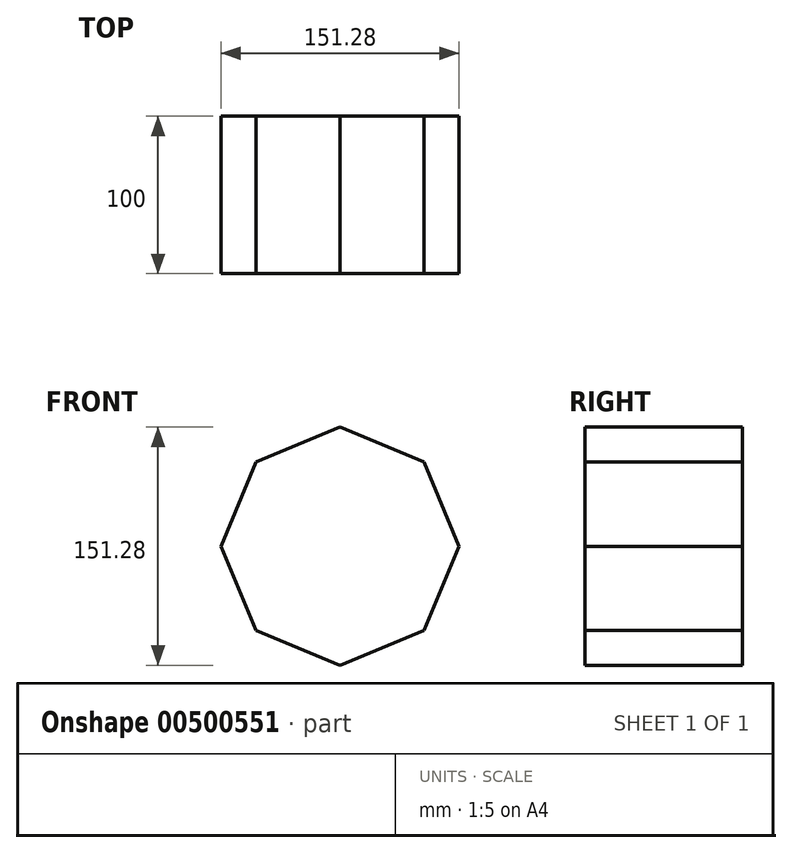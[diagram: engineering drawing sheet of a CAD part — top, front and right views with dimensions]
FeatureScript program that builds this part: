
annotation { "Feature Type Name" : "Feature", "Feature Type Description" : "" }
export const myFeature = defineFeature(function(context is Context, id is Id, definition is map)
    precondition{}
    {
        {
            var Q0;
            Q0=qCreatedBy(makeId("Front.planeOp"),FACE);
            var sketch = newSketch(context, id + "F0", { "sketchPlane" : qUnion([Q0])});
            skCircle(sketch, "E0.cCircle", {"center": v(0, 0) * mm, "radius": 75.64 * mm, "construction": true});
            skLineSegment(sketch, "E0.0", {"start": v(0, 75.64) * mm, "end": v(53.48, 53.48) * mm});
            skLineSegment(sketch, "E0.1", {"start": v(53.48, 53.48) * mm, "end": v(75.64, 0) * mm});
            skLineSegment(sketch, "E0.2", {"start": v(75.64, 0) * mm, "end": v(53.48, -53.48) * mm});
            skLineSegment(sketch, "E0.3", {"start": v(53.48, -53.48) * mm, "end": v(0, -75.64) * mm});
            skLineSegment(sketch, "E0.4", {"start": v(0, -75.64) * mm, "end": v(-53.48, -53.48) * mm});
            skLineSegment(sketch, "E0.5", {"start": v(-53.48, -53.48) * mm, "end": v(-75.64, 0) * mm});
            skLineSegment(sketch, "E0.6", {"start": v(-75.64, 0) * mm, "end": v(-53.48, 53.48) * mm});
            skLineSegment(sketch, "E0.7", {"start": v(-53.48, 53.48) * mm, "end": v(0, 75.64) * mm});
            skSolve(sketch);
        }
        {
            var Q0;
            Q0=makeQuery(id+"F0.imprint","IMPRINT",FACE,{"disambiguationData":[TD([[makeQuery(id+"F0.imprint","IMPRINT",EDGE,{"derivedFrom":sQuery(id+"F0.wireOp",EDGE,"E0.0")}),-1.0]])]});
            extrude(context, id + "F1", {"entities" : qUnion([Q0]), "depth" : 100 * mm});
        }
    });
